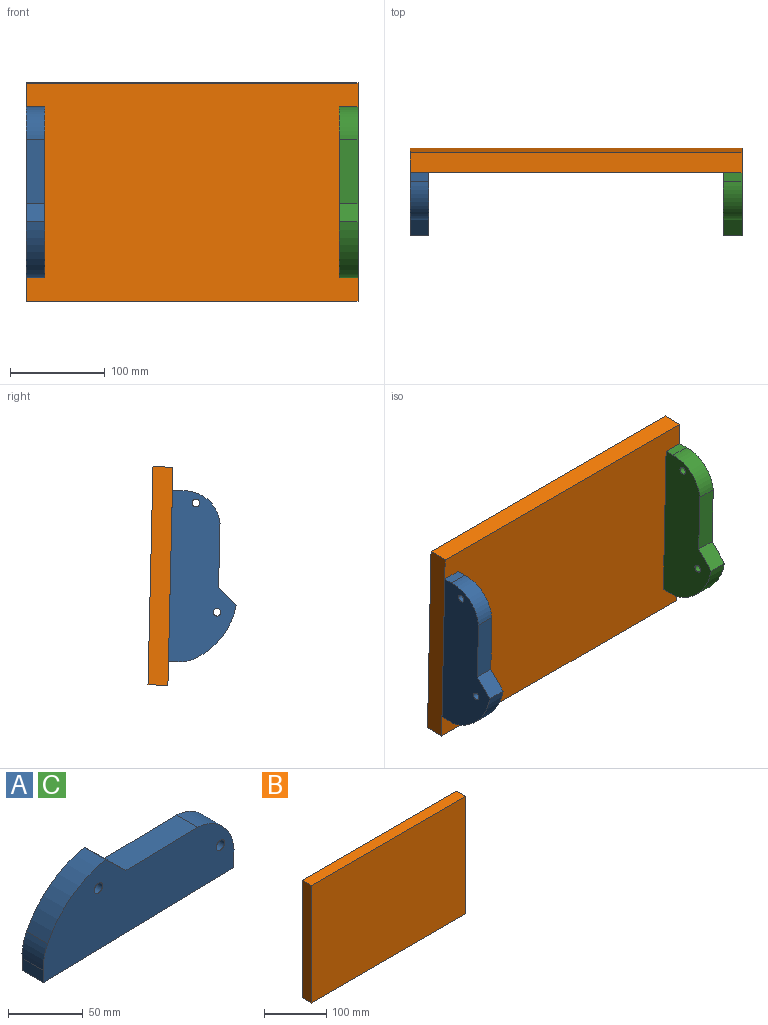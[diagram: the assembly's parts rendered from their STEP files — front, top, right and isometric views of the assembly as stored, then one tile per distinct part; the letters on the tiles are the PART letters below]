
ASSEMBLY  parts=3 mates=2
PART A: 12 faces, bbox 180.4x20x71.2 mm
  f0: plane 20x10mm, normal (-1,0,-0.02), area 200mm2, adj f1,f9,f10,f11
  f1: plane 180x20mm, normal (0.02,0,-1), area 3601mm2, adj f0,f2,f10,f11
  f2: plane 20x10mm, normal (1,0,0), area 200mm2, adj f1,f3,f10,f11
  f3: cylinder r=37.78mm len=40.22mm, axis (0,1,0), area 1173.2mm2, adj f2,f4,f10,f11
  f4: plane 67.57x20mm, normal (-0.02,0,1), area 1351.8mm2, adj f3,f5,f10,f11
  f5: plane 20x19.08mm, normal (0.69,0,0.72), area 530.3mm2, adj f4,f6,f10,f11
  f6: cylinder r=76.22mm len=54.84mm, axis (0,1,0), area 1425.8mm2, adj f5,f9,f10,f11
  f7: cylinder r=4mm len=20mm, axis (0,1,0), area 502.7mm2, adj f10,f11
  f8: cylinder r=4mm len=20mm, axis (0,1,0), area 502.7mm2, adj f10,f11
  f9: cylinder r=37.96mm len=20mm, axis (0,1,0), area 410.4mm2, adj f0,f6,f10,f11
  f10: plane 180.38x71.22mm, normal (0,-1,0), area 9157mm2, adj f0,f1,f2,f3,f4,f5,f6,f7
  f11: plane 180.38x71.22mm, normal (0,1,0), area 9157mm2, adj f0,f1,f2,f3,f4,f5,f6,f7
PART B: 6 faces, bbox 350x21x230 mm
  f0: plane 350x21mm, normal (0,0,1), area 7350mm2, adj f1,f3,f4,f5
  f1: plane 230x21mm, normal (-1,0,0), area 4830mm2, adj f0,f2,f4,f5
  f2: plane 350x21mm, normal (0,0,-1), area 7350mm2, adj f1,f3,f4,f5
  f3: plane 230x21mm, normal (1,0,0), area 4830mm2, adj f0,f2,f4,f5
  f4: plane 350x230mm, normal (0,-1,0), area 80500mm2, adj f0,f1,f2,f3
  f5: plane 350x230mm, normal (0,1,0), area 80500mm2, adj f0,f1,f2,f3
PART C: same geometry as A
PLACE A rot(axis=(0.58,-0.58,0.58),120deg) t=(-115.01,-84.43,85.99)mm
PLACE B rot(axis=(1,0,0),1.3deg) t=(59.99,-25.51,7.23)mm
PLACE C rot(axis=(0.58,-0.58,0.58),120deg) t=(214.99,-84.43,85.99)mm
MATE fastened C.f1 <-> B.f4  axis (0,1,0.02) through (234.99,-46.5,6.75)mm
MATE fastened B.f4 <-> A.f1  axis (0,-1,-0.02) through (-115.01,-46.5,6.75)mm
